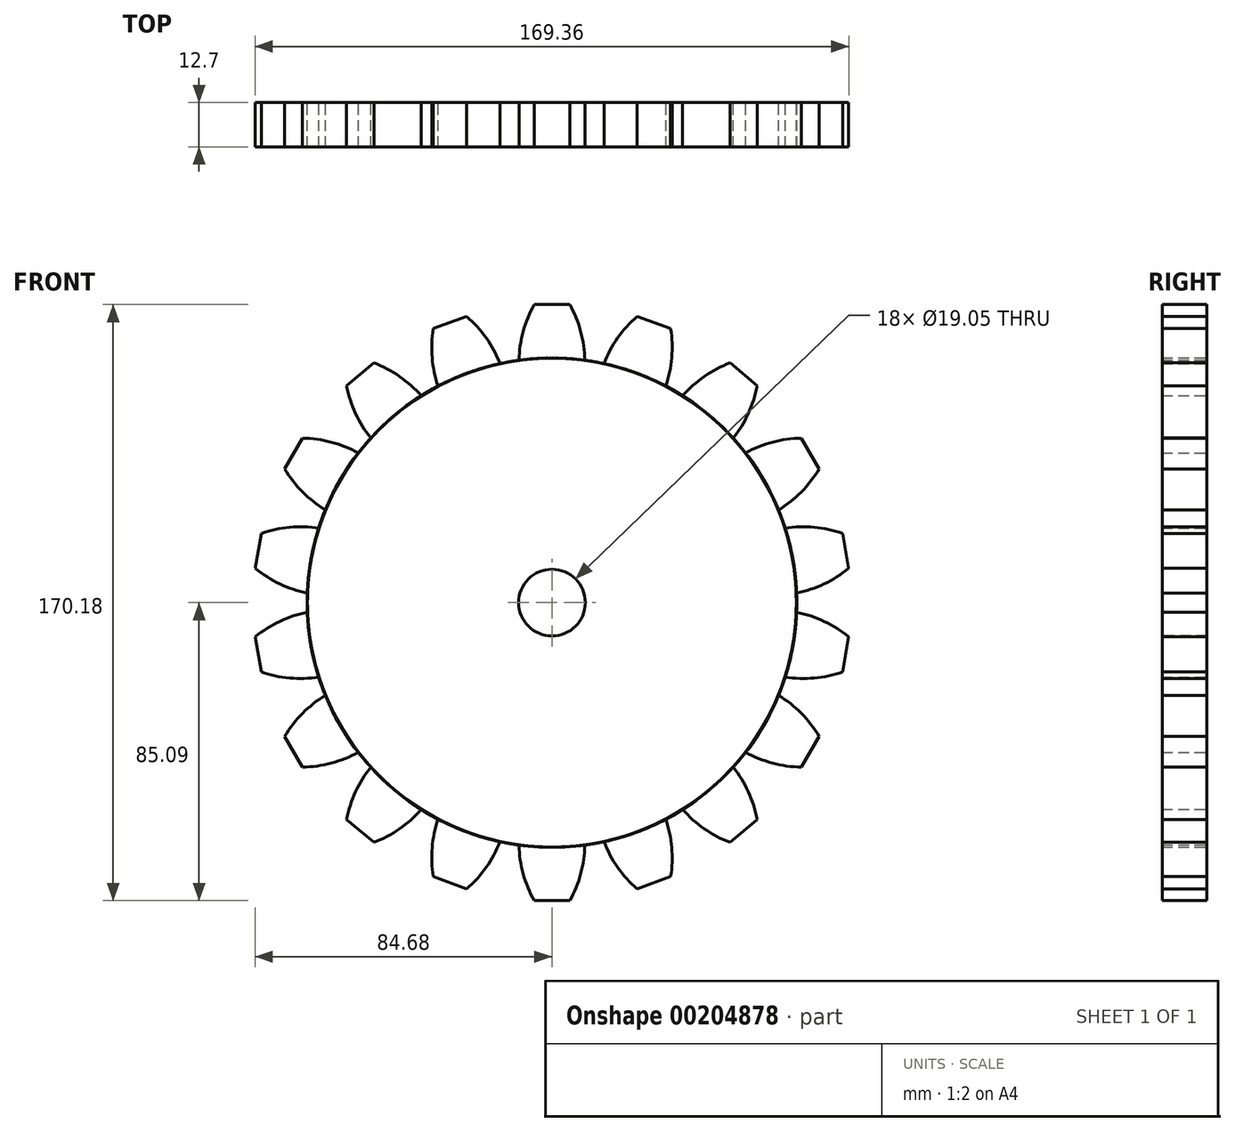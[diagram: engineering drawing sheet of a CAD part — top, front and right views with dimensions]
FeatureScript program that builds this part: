
annotation { "Feature Type Name" : "Feature", "Feature Type Description" : "" }
export const myFeature = defineFeature(function(context is Context, id is Id, definition is map)
    precondition{}
    {
        {
            var Q0;
            Q0=qCreatedBy(makeId("Front.planeOp"),FACE);
            var sketch = newSketch(context, id + "F0", { "sketchPlane" : qUnion([Q0])});
            skCircle(sketch, "E0", {"center": v(0, 0) * mm, "radius": 69.85 * mm});
            skLineSegment(sketch, "E1", {"start": v(0, 63.5) * mm, "end": v(0, 76.56) * mm});
            skPoint(sketch, "E2.orphan", {"position": v(0, 79.38) * mm});
            skLineSegment(sketch, "E3", {"start": v(-5.08, 85.1) * mm, "end": v(5.08, 85.1) * mm});
            skArc(sketch, "E4", {"start": v(-5.08, 85.1) * mm, "mid": v(-8.2, 77.42) * mm, "end": v(-9.4, 69.21) * mm});
            skArc(sketch, "E5", {"start": v(9.4, 69.21) * mm, "mid": v(8.2, 77.42) * mm, "end": v(5.08, 85.1) * mm});
            skSolve(sketch);
        }
        {
            var Q0;
            {var subQ0=sQuery(id+"F0.wireOp",EDGE,"E0");var subQ1=makeQuery(id+"F0.imprint","INTERSECT",VERTEX,{"derivedFrom":[subQ0,sQuery(id+"F0.wireOp",EDGE,"71006099-3903-45b5-9a77-b499ab4f176b0.MirrorCS")]});Q0=makeQuery(id+"F0.imprint","IMPRINT",FACE,{"disambiguationData":[TD([[makeQuery(id+"F0.imprint","IMPRINT",EDGE,{"disambiguationData":[TD([[subQ1,-1.0]])],"derivedFrom":subQ0}),1.0]])]});}
            var Q1;
            {var subQ0=sQuery(id+"F0.wireOp",EDGE,"HawqoFfQ-vyjP-PbXt-iczL-HoAtEcr3KnTR");Q1=makeQuery(id+"F0.imprint","IMPRINT",FACE,{"disambiguationData":[TD([[makeQuery(id+"F0.imprint","IMPRINT",EDGE,{"derivedFrom":subQ0}),1.0]])]});}
            var Q2;
            {var subQ0=sQuery(id+"F0.wireOp",EDGE,"71006099-3903-45b5-9a77-b499ab4f176b0.MirrorCS");Q2=makeQuery(id+"F0.imprint","IMPRINT",FACE,{"disambiguationData":[TD([[makeQuery(id+"F0.imprint","IMPRINT",EDGE,{"derivedFrom":subQ0}),-1.0]])]});}
            var Q3;
            Q3=makeQuery(id+"F0.imprint","IMPRINT",FACE,{"disambiguationData":[TD([[makeQuery(id+"F0.imprint","IMPRINT",EDGE,{"derivedFrom":sQuery(id+"F0.wireOp",EDGE,"E3")}),-1.0]])]});
            extrude(context, id + "F1", {"entities" : qUnion([Q0, Q1, Q2, Q3]), "endBound" : BoundingType.SYMMETRIC, "depth" : 12.7 * mm});
        }
        {
            var Q0;
            Q0=makeQuery(id+"F1.opExtrude","SWEPT_BODY",BODY,{"disambiguationData":[OSD([sQuery(id+"F0.wireOp",EDGE,"E0"),sQuery(id+"F0.wireOp",EDGE,"HawqoFfQ-vyjP-PbXt-iczL-HoAtEcr3KnTR"),sQuery(id+"F0.wireOp",EDGE,"71006099-3903-45b5-9a77-b499ab4f176b0.MirrorCS")])]});
            var Q1;
            Q1=makeQuery(id+"F1.opExtrude","SWEPT_FACE",FACE,{"disambiguationData":[OSD([sQuery(id+"F0.wireOp",EDGE,"E0")])]});
            circularPattern(context, id + "F2", {"entities" : qUnion([Q0]), "axis" : qUnion([Q1]), "angle" : 360 * degree, "instanceCount" : 18, "oppositeDirection" : true, "equalSpace" : true});
        }
        {
            var Q0;
            Q0=makeQuery(id+"F1.opExtrude","CAP_FACE",FACE,{"disambiguationData":[OSD([sQuery(id+"F0.wireOp",EDGE,"E0"),sQuery(id+"F0.wireOp",EDGE,"E3"),sQuery(id+"F0.wireOp",EDGE,"E4"),sQuery(id+"F0.wireOp",EDGE,"E5")])],"isStart":false});
            var sketch = newSketch(context, id + "F3", { "sketchPlane" : qUnion([Q0])});
            skCircle(sketch, "E6", {"center": v(0, 0) * mm, "radius": 9.53 * mm});
            skSolve(sketch);
        }
        {
            var Q0;
            Q0 = qSketchRegion(id + "F3", true);
            extrude(context, id + "F4", {"entities" : qUnion([Q0]), "operationType" : NewBodyOperationType.REMOVE, "endBound" : BoundingType.THROUGH_ALL, "oppositeDirection" : true, "depth" : 25.4 * mm});
        }
    });
